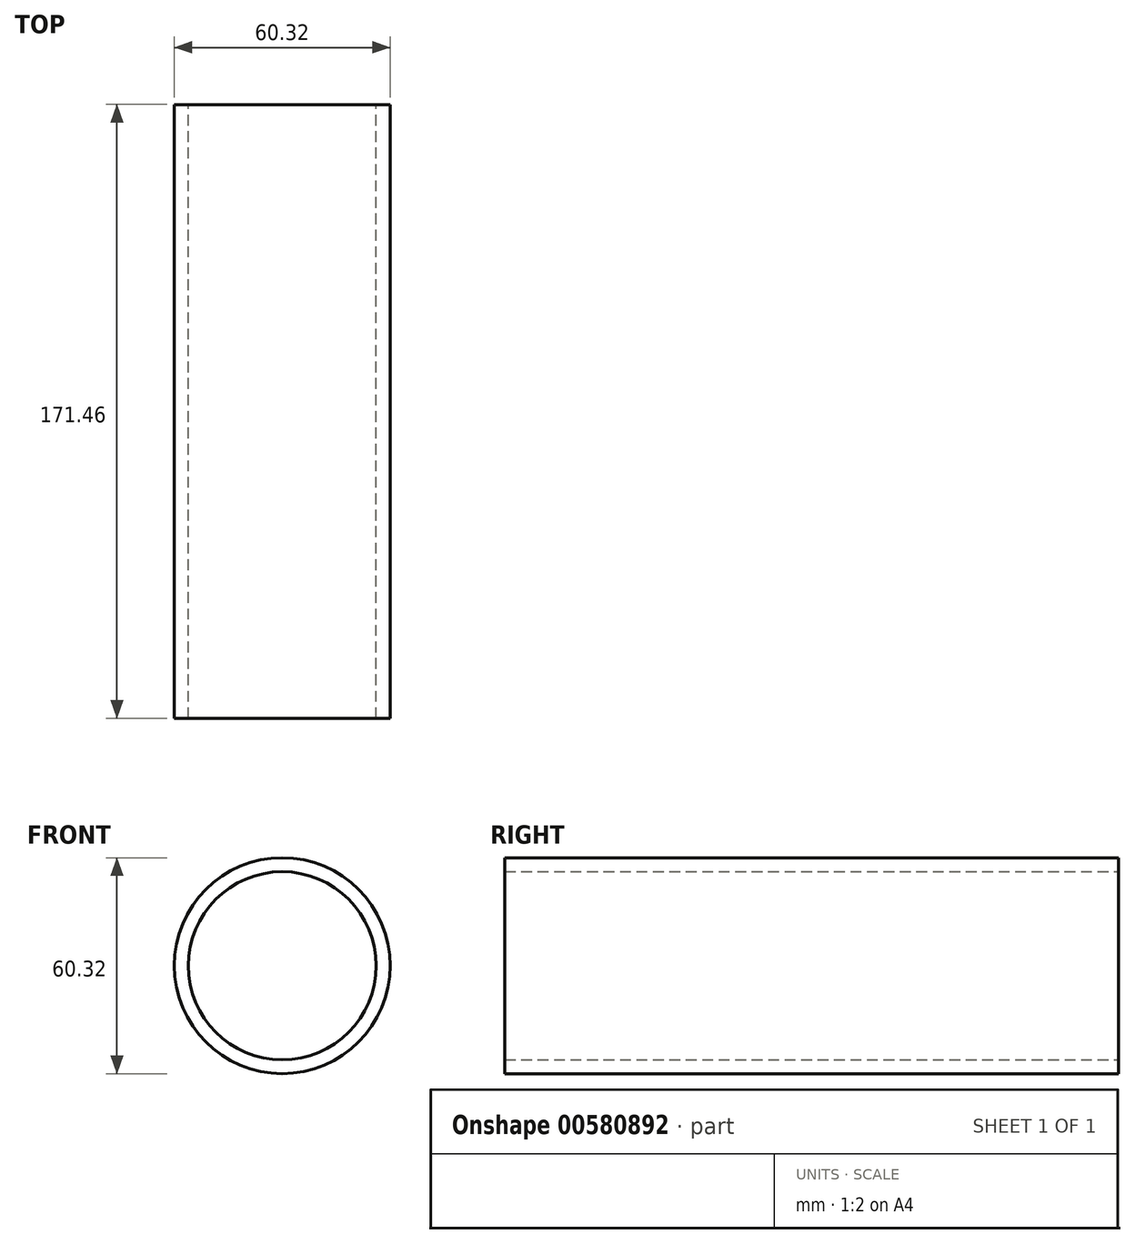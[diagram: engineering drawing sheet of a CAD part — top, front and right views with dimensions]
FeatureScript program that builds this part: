
annotation { "Feature Type Name" : "Feature", "Feature Type Description" : "" }
export const myFeature = defineFeature(function(context is Context, id is Id, definition is map)
    precondition{}
    {
        {
            var Q0;
            Q0=qCreatedBy(makeId("Front.planeOp"),FACE);
            var sketch = newSketch(context, id + "F0", { "sketchPlane" : qUnion([Q0])});
            skCircle(sketch, "E0", {"center": v(0, 0) * mm, "radius": 30.16 * mm});
            skCircle(sketch, "E1.0", {"center": v(0, 0) * mm, "radius": 26.25 * mm});
            skSolve(sketch);
        }
        {
            var Q0;
            Q0 = qSketchRegion(id + "F0", true);
            extrude(context, id + "F1", {"entities" : qUnion([Q0]), "endBound" : BoundingType.SYMMETRIC, "depth" : 171.45 * mm, "offsetDistance" : 25 * mm});
        }
    });
